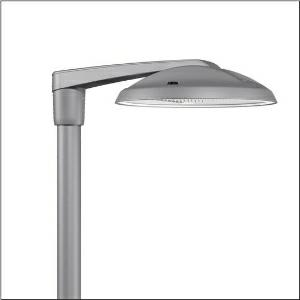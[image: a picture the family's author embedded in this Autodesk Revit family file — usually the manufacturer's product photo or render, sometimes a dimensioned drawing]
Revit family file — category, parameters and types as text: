
# Revit family: dl_50_iq_mini___st1_0a_5xa248d31v08le_d13a
name_source: partatom
category: Lighting Fixtures
units: mm (PartAtom-declared; Revit-internal decimal feet)

## family parameters
Cut with Voids When Loaded = No
Host = Face
Light Source = No
Part Type = Normal
Room Calculation Point = No
Round Connector Dimension = Use Diameter
Shared = No

## types (1)
- --- (1 x LED, 10390 lm, 66 W, 3000K)
    Apparent Load = 66 VA
    CIE Flux Codes = 37 72 97 100 100
    Color Rendering = 70
    Color Temperature = 3000K
    Default Elevation = 1800 mm
    Description = DL 50 iQ mini, mast luminaire, primary light control with lens, of PMMA, primary optical cover: cover, of toughened safety glass, transparent, light distribution: ST1.0a, light emission: direct distribution, primary light characteristic: asymmetric, installation type: post-top, side-entry, LED, High Power LED, rated luminous flux: 10.390lm, luminous efficacy: 157lm/W, light colour: 730, colour temperature: 3000K, control gear: iQ-Street Remote, D4i with power reduction, control: optimised constant luminous flux control (CLO 2.0), Desk-Remote (wireless, voltage-free reading and setting of iQ features in the workshop via application-optimized NFC function/RFID function), Light-Fading, Smart-Wire, Night-Set, Lumen-Switch, Temp-Guard, Auto-Match, Street-Remote, pre-setting: logarithmic dimming characteristic, mains connection: 230..240V, AC, 50/60Hz, connection cable pre-assembled, cable length: 8,5m, start of lifetime: 66W, end of service life: 69W, reduction: 30W, luminaire housing, of diecast aluminium, powder-coated, SITECO metallic grey (DB 702S), inclination adjustable: 0°, 5°, 10° (post-top) | 0°, -5°, -10°, -15° (side-entry), please order mast post-top element or mast side-entry element separately, diameter: 500mm, height: 115mm, post-top: for spigot size d x l = 76 x 100mm; with reducer (optional accessory) 60 x 100mm | side-entry: for spigot size d x l = 60 x 100mm; with reducer (optional accessory) 42 x 100mm, mounting height: 4..6m, Smart Interface above, protection rating (complete): IP66, insulation class (complete): insulation class II (safety insulation), certification: CE, ENEC, ENEC+, VDE, impact resistance: IK08, permissible operating ambient temperature for outdoor applications: -25..+40°C, standard-compliant lighting for roads and squares, packaging unit: 1 piece

Light Distribution: ST1.0a
    Height = 115 mm
    Lamp = 1 x LED
    Lamp Light Flux = 10390 lm
    Lamp Power = 66 W
    Lamp count = 1
    Length = 500 mm
    Luminous efficacy = 157 lm/W
    Manufacturer = Siteco
    ModVariant = No
    Model = 5XA248D31V08LE
    Number of Poles = 1
    OnlyDefault = Yes
    Power Factor = 1
    Product Name = DL 50 iQ mini | ST1.0a
    Product group = mast luminaire | pylon top
    ProductGroupID = 6100
    Protection Class = Protection class II
    Protection Degree = IP 66
    RLX_Detail_Level = 1
    RLX_Emergency_Light_Flux = 0 lm
    RLX_Emergency_Type = 0
    RLX_Emergency_Type_DB = No
    RlxData = <blob elided: 107161 chars, md5=f0fa7cde>
    Socket = socket
    Standby Power = 0 W
    System Light Flux = 10390 lm
    System Power = 66 W
    Type Comments = factory setting: luminous flux: 100 % | dim-lin: 254 | 691 mA
    Type Image = l_1251788.jpg
    URL = http://relux.com
    VarID = @adj_075153
    Voltage = 0 V
    Weight = 0.00 kg
    Width = 0 mm  [stored 0 ft]

note: [stored X ft] marks values corroborated as IEEE doubles in the binary element streams (Revit-internal decimal feet)

## geometry (parser evidence)
native form markers: Blend x4, Sweep x9
no freeform markers — native parametric forms only
